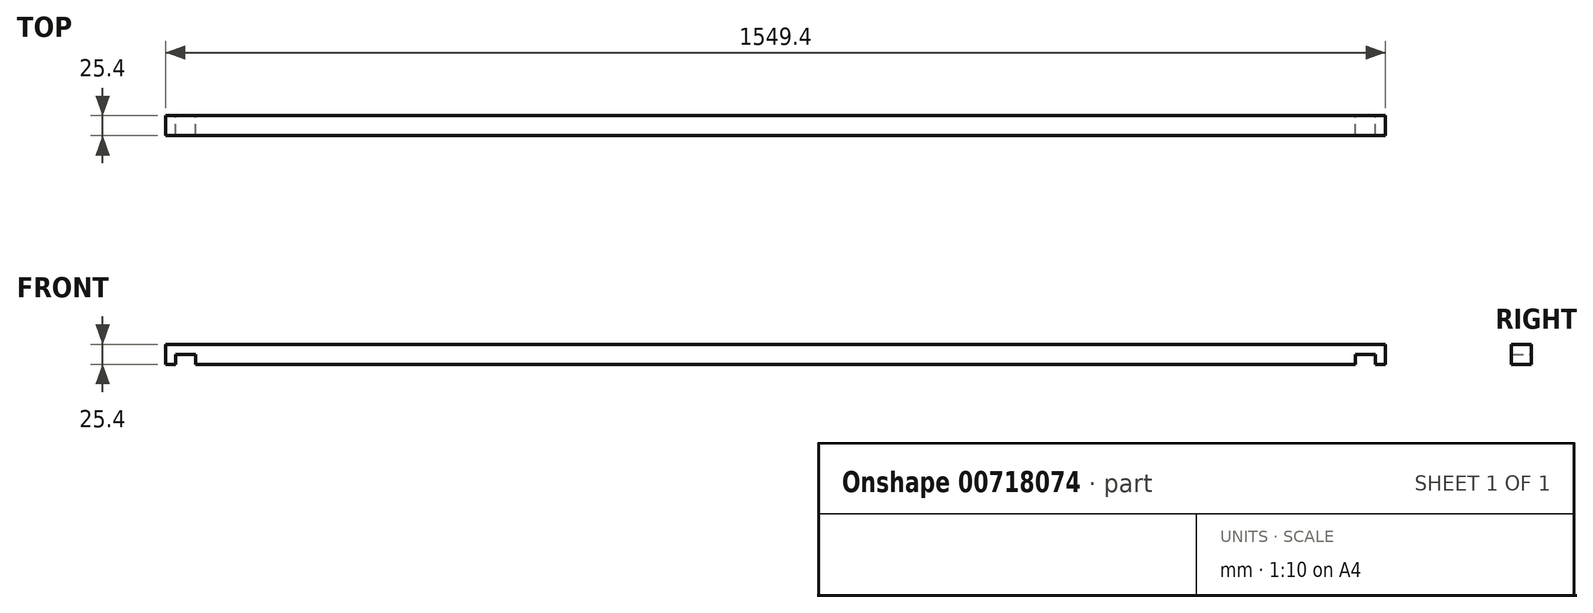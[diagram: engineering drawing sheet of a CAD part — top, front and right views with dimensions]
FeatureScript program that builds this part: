
annotation { "Feature Type Name" : "Feature", "Feature Type Description" : "" }
export const myFeature = defineFeature(function(context is Context, id is Id, definition is map)
    precondition{}
    {
        {
            var Q0;
            Q0=qCreatedBy(makeId("Front.planeOp"),FACE);
            var sketch = newSketch(context, id + "F0", { "sketchPlane" : qUnion([Q0])});
            skLineSegment(sketch, "E0.bottom", {"start": v(774.7, -12.7) * mm, "end": v(762, -12.7) * mm});
            skLineSegment(sketch, "E0.top", {"start": v(774.7, 12.7) * mm, "end": v(-774.7, 12.7) * mm});
            skLineSegment(sketch, "E0.left", {"start": v(774.7, -12.7) * mm, "end": v(774.7, 12.7) * mm});
            skLineSegment(sketch, "E0.right", {"start": v(-774.7, -12.7) * mm, "end": v(-774.7, 12.7) * mm});
            skPoint(sketch, "E0.middle", {"position": v(0, 0) * mm});
            skLineSegment(sketch, "E1.top", {"start": v(-762, 0) * mm, "end": v(-736.6, 0) * mm});
            skLineSegment(sketch, "E1.left", {"start": v(-762, -12.7) * mm, "end": v(-762, 0) * mm});
            skLineSegment(sketch, "E1.right", {"start": v(-736.6, -12.7) * mm, "end": v(-736.6, 0) * mm});
            skLineSegment(sketch, "E2.trimOffspring", {"start": v(-762, -12.7) * mm, "end": v(-774.7, -12.7) * mm});
            skLineSegment(sketch, "E3.top", {"start": v(762, 0) * mm, "end": v(736.6, 0) * mm});
            skLineSegment(sketch, "E3.left", {"start": v(762, -12.7) * mm, "end": v(762, 0) * mm});
            skLineSegment(sketch, "E3.right", {"start": v(736.6, -12.7) * mm, "end": v(736.6, 0) * mm});
            skLineSegment(sketch, "E4.trimOffspring", {"start": v(736.6, -12.7) * mm, "end": v(-736.6, -12.7) * mm});
            skSolve(sketch);
        }
        {
            var Q0;
            Q0 = qSketchRegion(id + "F0", true);
            extrude(context, id + "F1", {"entities" : qUnion([Q0]), "depth" : 25.4 * mm, "offsetDistance" : 25.4 * mm});
        }
    });
